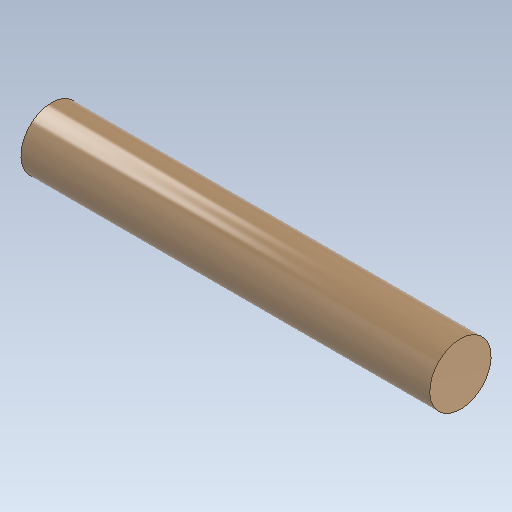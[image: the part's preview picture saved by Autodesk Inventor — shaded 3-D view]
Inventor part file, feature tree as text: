
AUTODESK INVENTOR PART (.ipt)
format: ipt  version: 2020.5 (Build 245400000, 400)  size: 92,160 bytes
history: native  units: mm
features: extrude x1, sketch x1
ambient origin geometry x8: Origin, YZ Plane, XZ Plane, XY Plane, X Axis, Y Axis, Z Axis, Center Point
bodies: Body1 (feature_tree)
feature tree (2):
  extrude  "Extrusion3"  Depth=20.0mm TaperAngle=0.0deg
  sketch  "Sketch3"  dims[d8=3.0mm d9=20.0mm d10=0.0mm]
